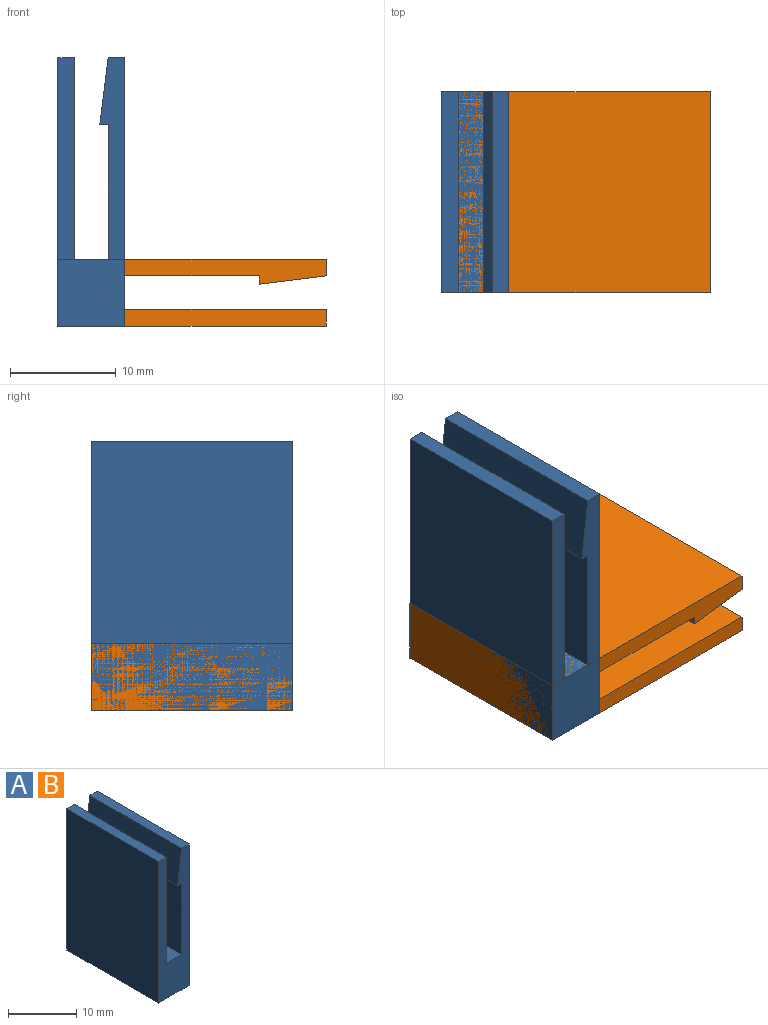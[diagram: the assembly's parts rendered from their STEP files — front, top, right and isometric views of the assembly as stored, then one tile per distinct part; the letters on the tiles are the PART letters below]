
ASSEMBLY  parts=2 mates=1
PART A: 12 faces, bbox 6.4x19.1x25.4 mm
  f0: plane 19.05x3.18mm, normal (0,0,1), area 60.5mm2, adj f1,f9,f10,f11
  f1: plane 19.05x19.05mm, normal (1,0,0), area 362.9mm2, adj f0,f2,f10,f11
  f2: plane 19.05x1.59mm, normal (0,0,1), area 30.2mm2, adj f1,f3,f10,f11
  f3: plane 25.4x19.05mm, normal (-1,0,0), area 483.9mm2, adj f2,f4,f10,f11
  f4: plane 19.05x6.35mm, normal (0,0,-1), area 121mm2, adj f3,f5,f10,f11
  f5: plane 25.4x19.05mm, normal (1,0,0), area 483.9mm2, adj f4,f6,f10,f11
  f6: plane 19.05x1.59mm, normal (0,0,1), area 30.2mm2, adj f5,f7,f10,f11
  f7: plane 19.05x6.35mm, normal (-0.99,0,0.12), area 121.9mm2, adj f6,f8,f10,f11
  f8: plane 19.05x0.79mm, normal (0,0,-1), area 15.1mm2, adj f7,f9,f10,f11
  f9: plane 19.05x12.7mm, normal (-1,0,0), area 241.9mm2, adj f0,f8,f10,f11
  f10: plane 25.4x6.35mm, normal (0,-1,0), area 103.3mm2, adj f0,f1,f2,f3,f4,f5,f6,f7
  f11: plane 25.4x6.35mm, normal (0,1,0), area 103.3mm2, adj f0,f1,f2,f3,f4,f5,f6,f7
PART B: same geometry as A
PLACE A t=(9.55,3.15,-32.63)mm
PLACE B rot(axis=(0.71,0,0.71),180deg) t=(9.55,-15.9,-32.63)mm
MATE fastened B.f10 <-> A.f11  axis (0,1,0) through (9.55,3.15,-32.63)mm
